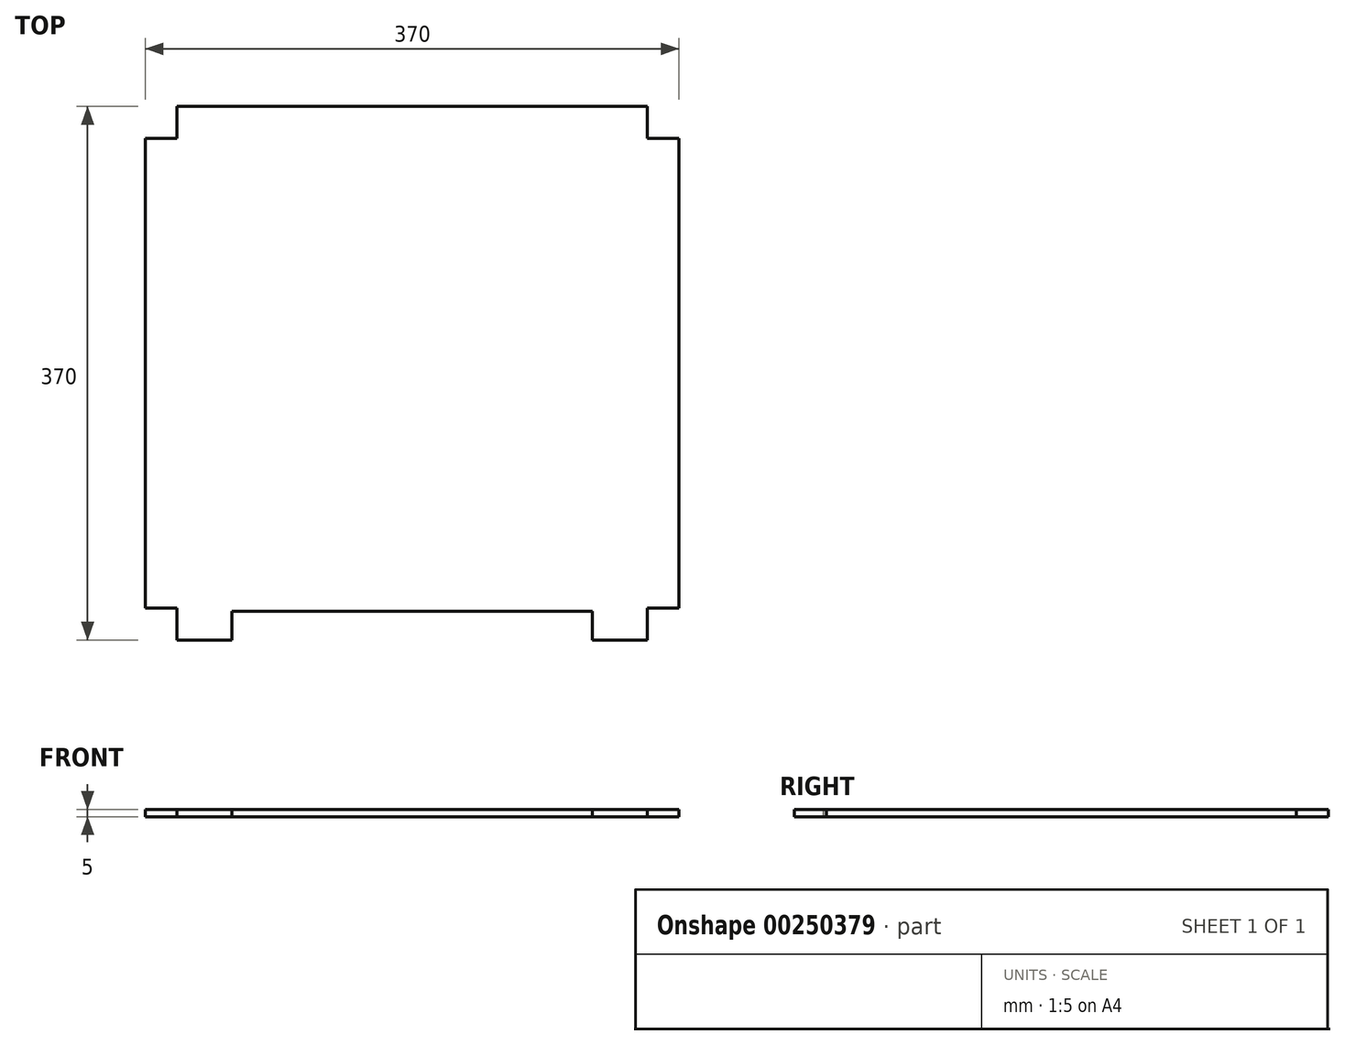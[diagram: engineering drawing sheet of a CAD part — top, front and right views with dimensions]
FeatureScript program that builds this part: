
annotation { "Feature Type Name" : "Feature", "Feature Type Description" : "" }
export const myFeature = defineFeature(function(context is Context, id is Id, definition is map)
    precondition{}
    {
        {
            var Q0;
            Q0=qCreatedBy(makeId("Top.planeOp"),FACE);
            var sketch = newSketch(context, id + "F0", { "sketchPlane" : qUnion([Q0])});
            skLineSegment(sketch, "E0.bottom", {"start": v(-185, 185) * mm, "end": v(185, 185) * mm, "construction": true});
            skLineSegment(sketch, "E0.top", {"start": v(-185, -185) * mm, "end": v(185, -185) * mm, "construction": true});
            skLineSegment(sketch, "E0.left", {"start": v(-185, 185) * mm, "end": v(-185, -185) * mm, "construction": true});
            skLineSegment(sketch, "E0.right", {"start": v(185, 185) * mm, "end": v(185, -185) * mm, "construction": true});
            skLineSegment(sketch, "E1.bottom", {"start": v(-185, 185) * mm, "end": v(-163, 185) * mm});
            skLineSegment(sketch, "E1.top", {"start": v(-185, 163) * mm, "end": v(-163, 163) * mm});
            skLineSegment(sketch, "E1.left", {"start": v(-185, 185) * mm, "end": v(-185, 163) * mm});
            skLineSegment(sketch, "E1.right", {"start": v(-163, 185) * mm, "end": v(-163, 163) * mm});
            skLineSegment(sketch, "E2.MirrorCS", {"start": v(163, 185) * mm, "end": v(163, 163) * mm});
            skLineSegment(sketch, "E3.MirrorCS", {"start": v(185, 163) * mm, "end": v(163, 163) * mm});
            skLineSegment(sketch, "E4.MirrorCS", {"start": v(185, 185) * mm, "end": v(185, 163) * mm});
            skLineSegment(sketch, "E5.MirrorCS", {"start": v(185, 185) * mm, "end": v(163, 185) * mm});
            skLineSegment(sketch, "E6.MirrorCS", {"start": v(-163, -185) * mm, "end": v(-163, -163) * mm});
            skLineSegment(sketch, "E7.MirrorCS", {"start": v(-185, -163) * mm, "end": v(-163, -163) * mm});
            skLineSegment(sketch, "E8.MirrorCS", {"start": v(-185, -185) * mm, "end": v(-185, -163) * mm});
            skLineSegment(sketch, "E9.MirrorCS", {"start": v(-185, -185) * mm, "end": v(-163, -185) * mm});
            skLineSegment(sketch, "E10.MirrorCS", {"start": v(185, -163) * mm, "end": v(163, -163) * mm});
            skLineSegment(sketch, "E11.MirrorCS", {"start": v(163, -185) * mm, "end": v(163, -163) * mm});
            skLineSegment(sketch, "E12.MirrorCS", {"start": v(185, -185) * mm, "end": v(163, -185) * mm});
            skLineSegment(sketch, "E13.MirrorCS", {"start": v(185, -185) * mm, "end": v(185, -163) * mm});
            skLineSegment(sketch, "E14", {"start": v(-163, 185) * mm, "end": v(163, 185) * mm});
            skLineSegment(sketch, "E15", {"start": v(185, 163) * mm, "end": v(185, -163) * mm});
            skLineSegment(sketch, "E16", {"start": v(163, -185) * mm, "end": v(-163, -185) * mm});
            skLineSegment(sketch, "E17", {"start": v(-185, -163) * mm, "end": v(-185, 163) * mm});
            skLineSegment(sketch, "E18.bottom", {"start": v(-125, -185) * mm, "end": v(125, -185) * mm});
            skLineSegment(sketch, "E18.top", {"start": v(-125, -165) * mm, "end": v(125, -165) * mm});
            skLineSegment(sketch, "E18.left", {"start": v(-125, -185) * mm, "end": v(-125, -165) * mm});
            skLineSegment(sketch, "E18.right", {"start": v(125, -185) * mm, "end": v(125, -165) * mm});
            skSolve(sketch);
        }
        {
            var Q0;
            Q0=makeQuery(id+"F0.imprint","IMPRINT",FACE,{"disambiguationData":[TD([[makeQuery(id+"F0.imprint","IMPRINT",EDGE,{"derivedFrom":sQuery(id+"F0.wireOp",EDGE,"E1.top")}),-1.0]])]});
            extrude(context, id + "F1", {"entities" : qUnion([Q0]), "depth" : 5 * mm});
        }
    });
